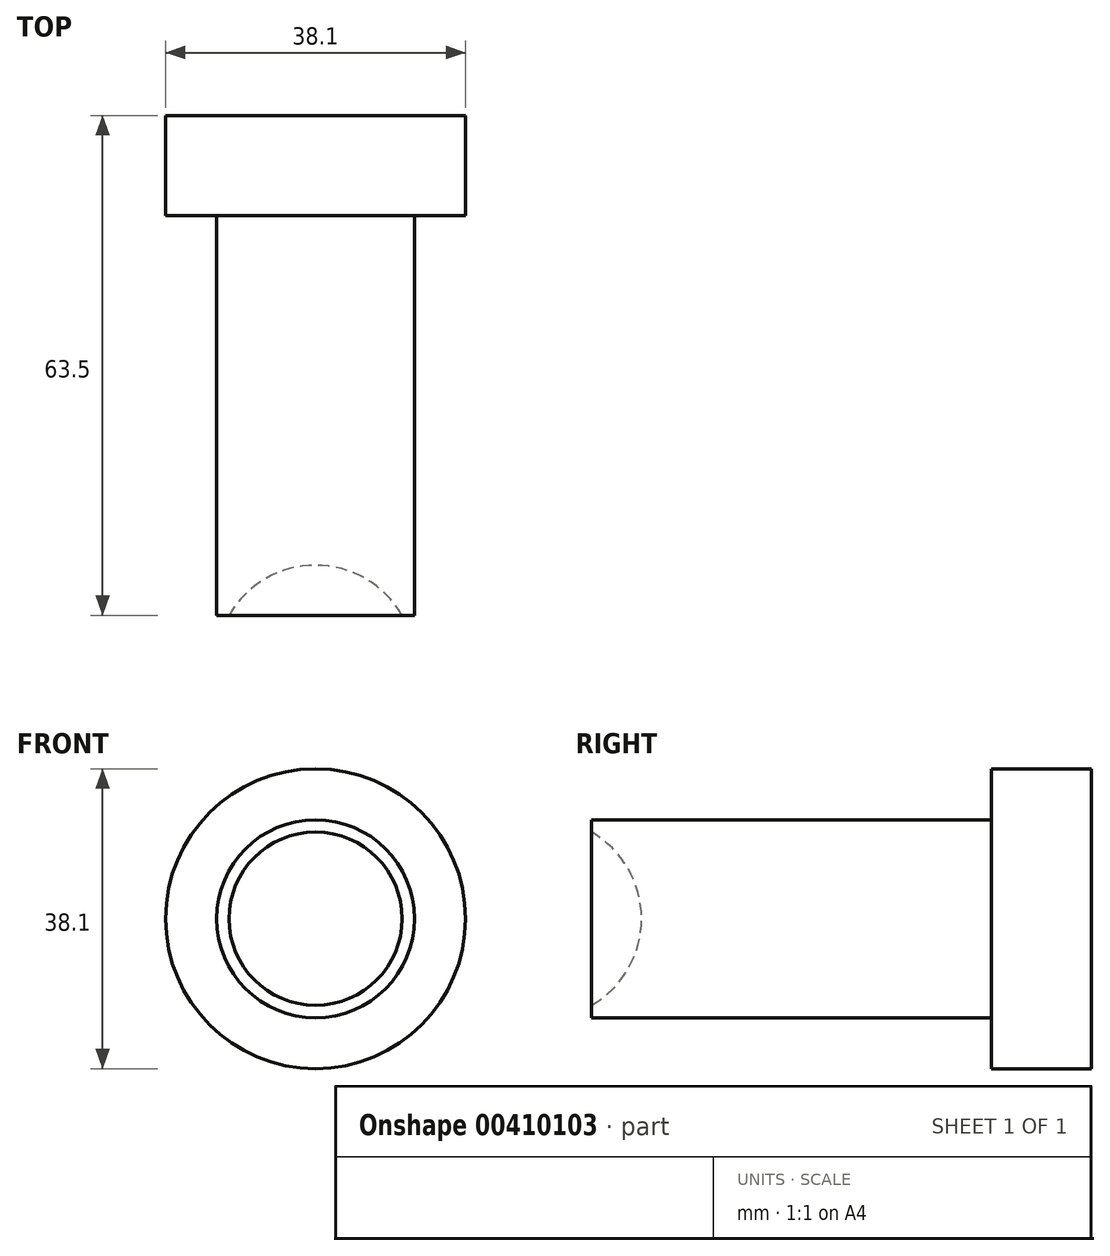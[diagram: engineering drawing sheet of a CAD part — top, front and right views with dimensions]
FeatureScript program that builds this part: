
annotation { "Feature Type Name" : "Feature", "Feature Type Description" : "" }
export const myFeature = defineFeature(function(context is Context, id is Id, definition is map)
    precondition{}
    {
        {
            var Q0;
            Q0=qCreatedBy(makeId("Front.planeOp"),FACE);
            var sketch = newSketch(context, id + "F0", { "sketchPlane" : qUnion([Q0])});
            skCircle(sketch, "E0", {"center": v(0, 0) * mm, "radius": 19.05 * mm});
            skSolve(sketch);
        }
        {
            var Q0;
            Q0=makeQuery(id+"F0.imprint","IMPRINT",FACE,{"disambiguationData":[TD([[makeQuery(id+"F0.imprint","IMPRINT",EDGE,{"derivedFrom":sQuery(id+"F0.wireOp",EDGE,"E0")}),1.0]])]});
            extrude(context, id + "F1", {"entities" : qUnion([Q0]), "depth" : 12.7 * mm});
        }
        {
            var Q0;
            Q0=makeQuery(id+"F1.opExtrude","CAP_FACE",FACE,{"disambiguationData":[OSD([sQuery(id+"F0.wireOp",EDGE,"E0")])],"isStart":false});
            var sketch = newSketch(context, id + "F2", { "sketchPlane" : qUnion([Q0])});
            skCircle(sketch, "E1", {"center": v(0, 0) * mm, "radius": 12.57 * mm});
            skSolve(sketch);
        }
        {
            var Q0;
            Q0 = qSketchRegion(id + "F2", true);
            extrude(context, id + "F3", {"entities" : qUnion([Q0]), "operationType" : NewBodyOperationType.ADD, "depth" : 50.8 * mm});
        }
        {
            var Q0;
            Q0=qCreatedBy(makeId("Right.planeOp"),FACE);
            var sketch = newSketch(context, id + "F4", { "sketchPlane" : qUnion([Q0])});
            skLineSegment(sketch, "E2", {"start": v(-12.7, -12.57) * mm, "end": v(-63.5, -12.57) * mm});
            skLineSegment(sketch, "E3", {"start": v(-63.5, 12.57) * mm, "end": v(-12.7, 12.57) * mm});
            skLineSegment(sketch, "E4", {"start": v(-69.85, 12.7) * mm, "end": v(-69.85, -12.7) * mm});
            skArc(sketch, "E5", {"start": v(-69.85, -12.7) * mm, "mid": v(-57.15, 0) * mm, "end": v(-69.85, 12.7) * mm});
            skSolve(sketch);
        }
        {
            var Q0;
            Q0=makeQuery(id+"F4.imprint","IMPRINT",FACE,{"disambiguationData":[TD([[makeQuery(id+"F4.imprint","IMPRINT",EDGE,{"derivedFrom":sQuery(id+"F4.wireOp",EDGE,"E4")}),1.0]])]});
            var Q1;
            Q1=sQuery(id+"F4.wireOp",EDGE,"E4");
            revolve(context, id + "F5", {"operationType" : NewBodyOperationType.REMOVE, "entities" : qUnion([Q0]), "axis" : qUnion([Q1]), "revolveType" : RevolveType.FULL, "oppositeDirection" : true});
        }
    });
